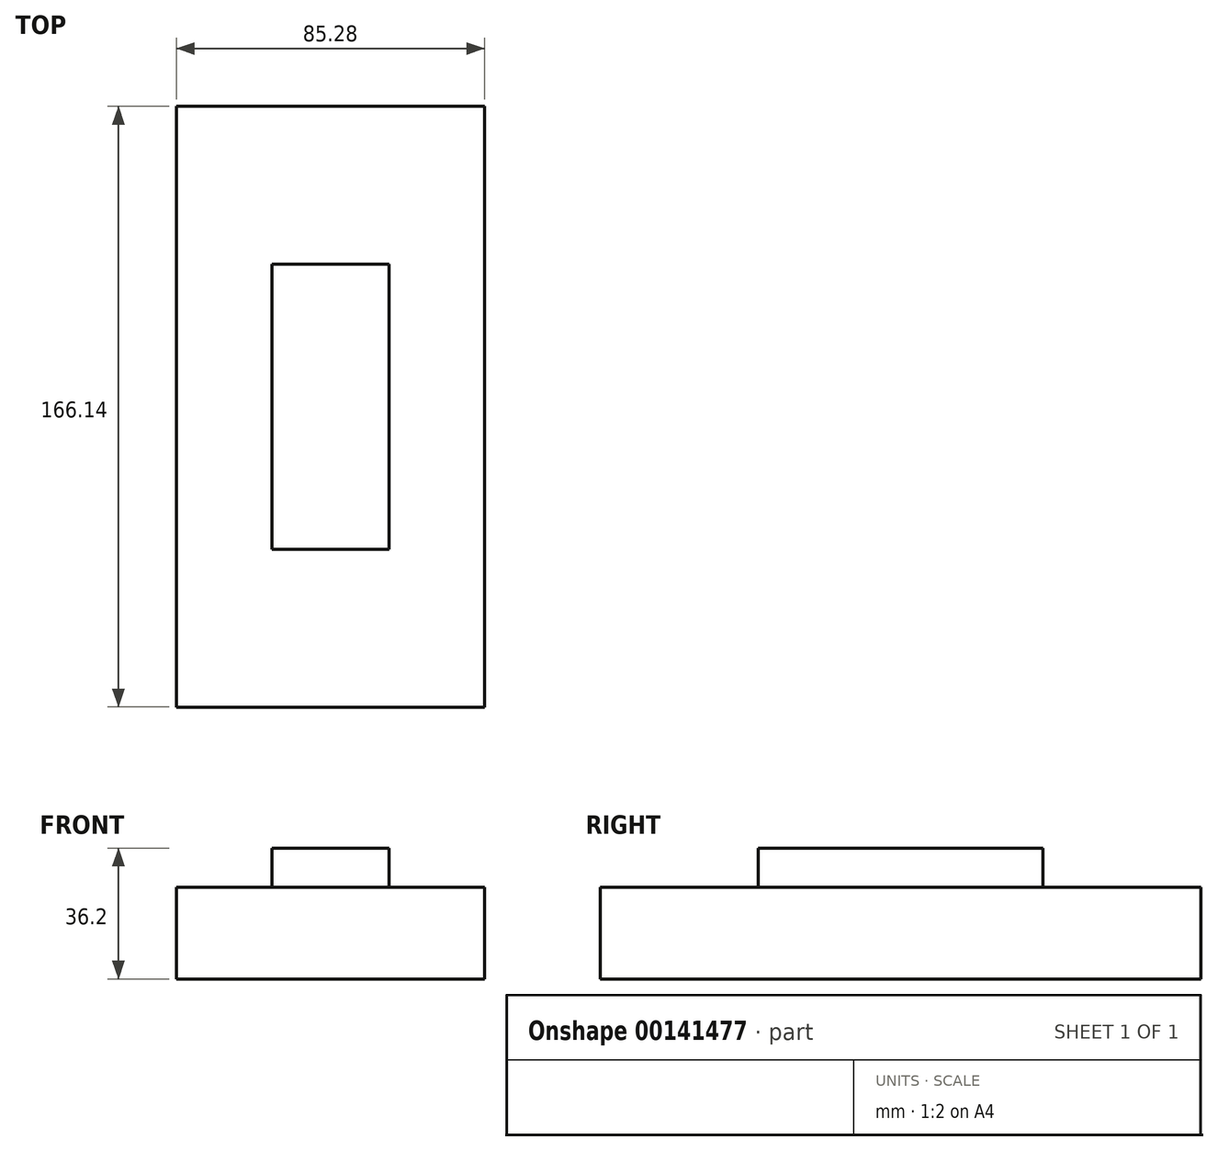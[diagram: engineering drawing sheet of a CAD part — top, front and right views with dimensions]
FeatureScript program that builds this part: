
annotation { "Feature Type Name" : "Feature", "Feature Type Description" : "" }
export const myFeature = defineFeature(function(context is Context, id is Id, definition is map)
    precondition{}
    {
        {
            var Q0;
            Q0=qCreatedBy(makeId("Top.planeOp"),FACE);
            var sketch = newSketch(context, id + "F0", { "sketchPlane" : qUnion([Q0])});
            skLineSegment(sketch, "E0.bottom", {"start": v(42.64, -83.07) * mm, "end": v(-42.64, -83.07) * mm});
            skLineSegment(sketch, "E0.top", {"start": v(42.64, 83.07) * mm, "end": v(-42.64, 83.07) * mm});
            skLineSegment(sketch, "E0.left", {"start": v(42.64, -83.07) * mm, "end": v(42.64, 83.07) * mm});
            skLineSegment(sketch, "E0.right", {"start": v(-42.64, -83.07) * mm, "end": v(-42.64, 83.07) * mm});
            skPoint(sketch, "E0.middle", {"position": v(0, 0) * mm});
            skSolve(sketch);
        }
        {
            var Q0;
            Q0=makeQuery(id+"F0.imprint","IMPRINT",FACE,{"disambiguationData":[TD([[makeQuery(id+"F0.imprint","IMPRINT",EDGE,{"derivedFrom":sQuery(id+"F0.wireOp",EDGE,"E0.bottom")}),-1.0]])]});
            extrude(context, id + "F1", {"entities" : qUnion([Q0]), "depth" : 25.4 * mm});
        }
        {
            var Q0;
            Q0=makeQuery(id+"F1.opExtrude","CAP_FACE",FACE,{"disambiguationData":[OSD([sQuery(id+"F0.wireOp",EDGE,"E0.bottom"),sQuery(id+"F0.wireOp",EDGE,"E0.top"),sQuery(id+"F0.wireOp",EDGE,"E0.left"),sQuery(id+"F0.wireOp",EDGE,"E0.right")])],"isStart":false});
            var sketch = newSketch(context, id + "F2", { "sketchPlane" : qUnion([Q0])});
            skLineSegment(sketch, "E1.bottom", {"start": v(16.2, -39.4) * mm, "end": v(-16.2, -39.4) * mm});
            skLineSegment(sketch, "E1.top", {"start": v(16.2, 39.4) * mm, "end": v(-16.2, 39.4) * mm});
            skLineSegment(sketch, "E1.left", {"start": v(16.2, -39.4) * mm, "end": v(16.2, 39.4) * mm});
            skLineSegment(sketch, "E1.right", {"start": v(-16.2, -39.4) * mm, "end": v(-16.2, 39.4) * mm});
            skPoint(sketch, "E1.middle", {"position": v(0, 0) * mm});
            skSolve(sketch);
        }
        {
            var Q0;
            Q0 = qSketchRegion(id + "F2", true);
            extrude(context, id + "F3", {"entities" : qUnion([Q0]), "operationType" : NewBodyOperationType.ADD, "depth" : 10.8 * mm});
        }
    });
